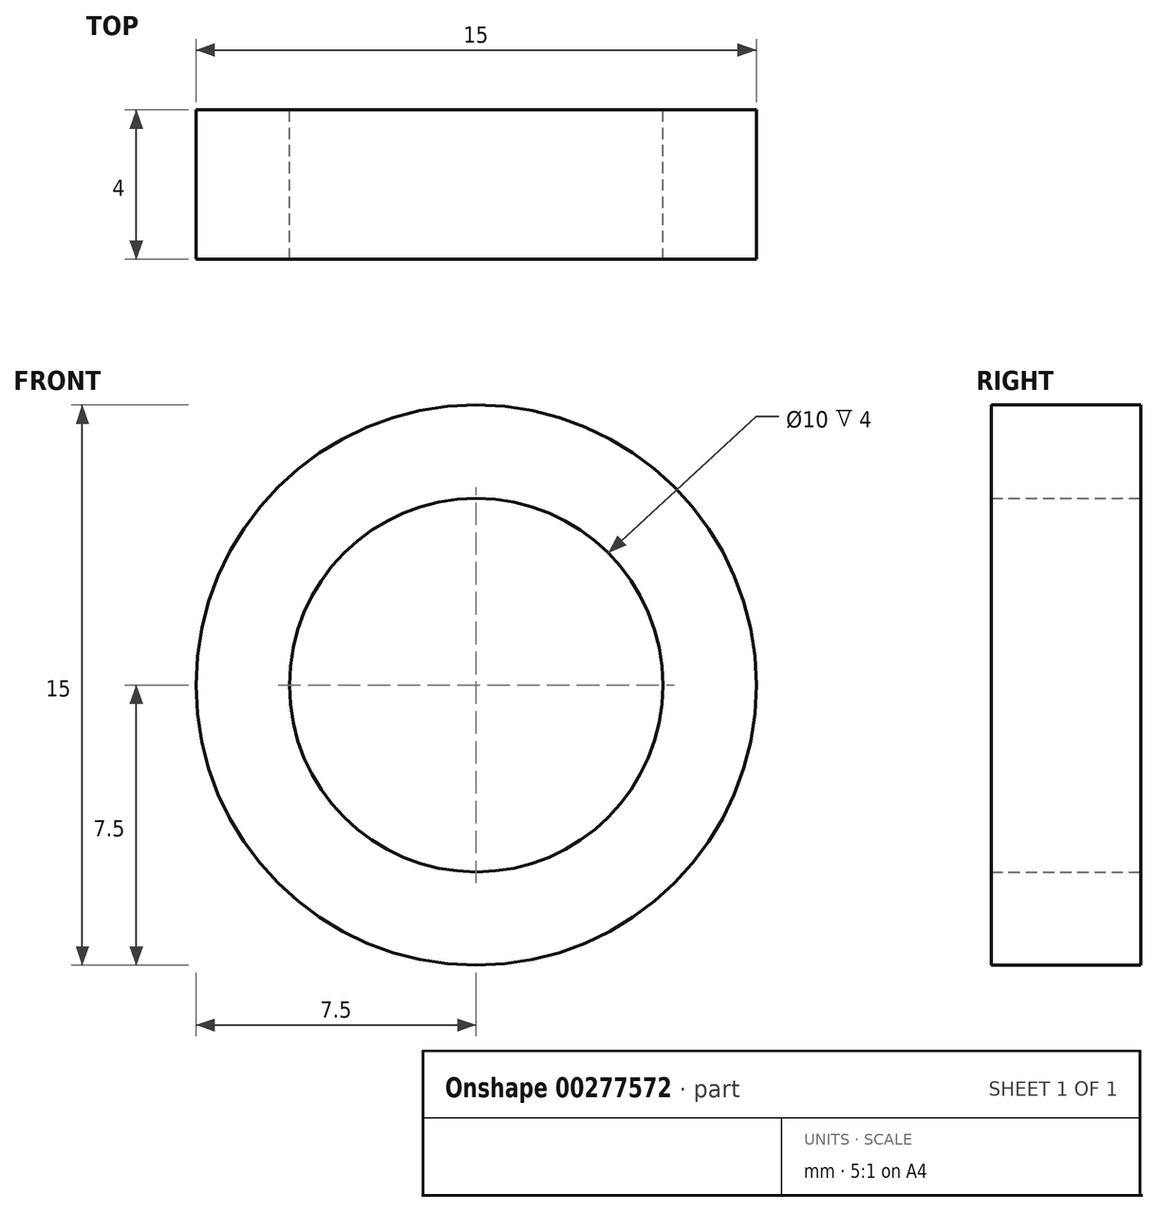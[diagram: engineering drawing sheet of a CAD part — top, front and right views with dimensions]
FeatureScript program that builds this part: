
annotation { "Feature Type Name" : "Feature", "Feature Type Description" : "" }
export const myFeature = defineFeature(function(context is Context, id is Id, definition is map)
    precondition{}
    {
        {
            var Q0;
            Q0=qCreatedBy(makeId("Front.planeOp"),FACE);
            var sketch = newSketch(context, id + "F0", { "sketchPlane" : qUnion([Q0])});
            skCircle(sketch, "E0", {"center": v(0, 0) * mm, "radius": 5 * mm});
            skCircle(sketch, "E1", {"center": v(0, 0) * mm, "radius": 7.5 * mm});
            skSolve(sketch);
        }
        {
            var Q0;
            Q0=makeQuery(id+"F0.imprint","IMPRINT",FACE,{"disambiguationData":[TD([[makeQuery(id+"F0.imprint","IMPRINT",EDGE,{"derivedFrom":sQuery(id+"F0.wireOp",EDGE,"E0")}),-1.0]])]});
            extrude(context, id + "F1", {"entities" : qUnion([Q0]), "depth" : 4 * mm, "offsetDistance" : 25 * mm});
        }
    });
